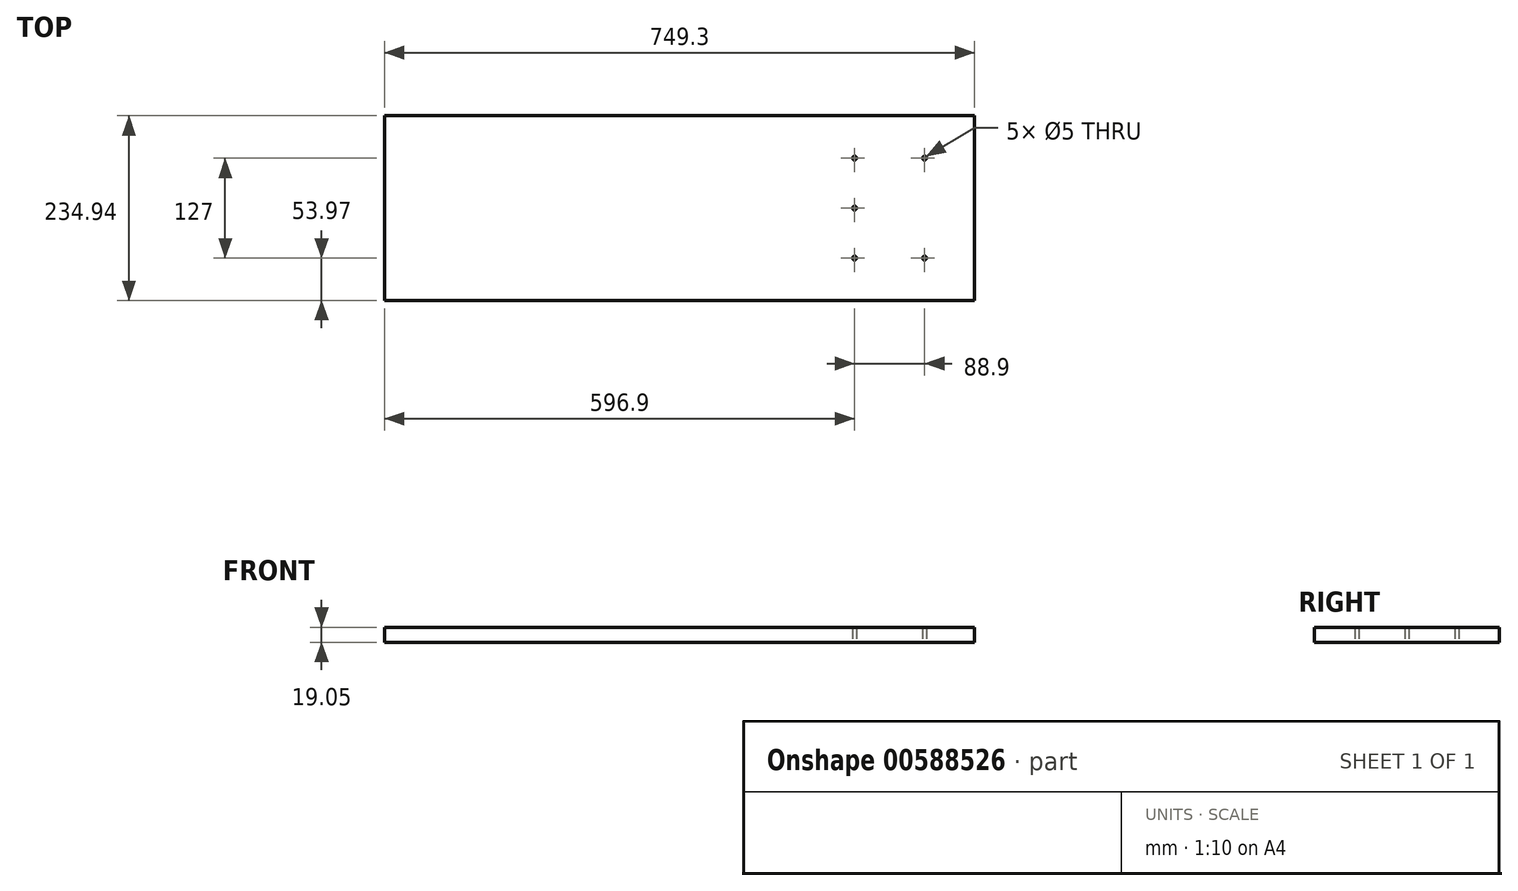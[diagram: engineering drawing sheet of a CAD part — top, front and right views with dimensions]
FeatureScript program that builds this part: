
annotation { "Feature Type Name" : "Feature", "Feature Type Description" : "" }
export const myFeature = defineFeature(function(context is Context, id is Id, definition is map)
    precondition{}
    {
        {
            var Q0;
            Q0=qCreatedBy(makeId("Top.planeOp"),FACE);
            var sketch = newSketch(context, id + "F0", { "sketchPlane" : qUnion([Q0])});
            skLineSegment(sketch, "E0.bottom", {"start": v(-374.65, 117.48) * mm, "end": v(374.65, 117.48) * mm});
            skLineSegment(sketch, "E0.top", {"start": v(-374.65, -117.47) * mm, "end": v(374.65, -117.47) * mm});
            skLineSegment(sketch, "E0.left", {"start": v(-374.65, 117.48) * mm, "end": v(-374.65, -117.47) * mm});
            skLineSegment(sketch, "E0.right", {"start": v(374.65, 117.48) * mm, "end": v(374.65, -117.47) * mm});
            skPoint(sketch, "E0.middle", {"position": v(0, 0) * mm});
            skCircle(sketch, "E1", {"center": v(311.15, 63.5) * mm, "radius": 2.5 * mm});
            skCircle(sketch, "E2.MirrorC", {"center": v(311.15, -63.5) * mm, "radius": 2.5 * mm});
            skCircle(sketch, "E3", {"center": v(222.25, 63.5) * mm, "radius": 2.5 * mm});
            skCircle(sketch, "E4", {"center": v(222.25, 0) * mm, "radius": 2.5 * mm});
            skCircle(sketch, "E5.MirrorC", {"center": v(222.25, -63.5) * mm, "radius": 2.5 * mm});
            skSolve(sketch);
        }
        {
            var Q0;
            Q0 = qSketchRegion(id + "F0", true);
            extrude(context, id + "F1", {"entities" : qUnion([Q0]), "depth" : 19.05 * mm, "offsetDistance" : 25.4 * mm});
        }
    });
